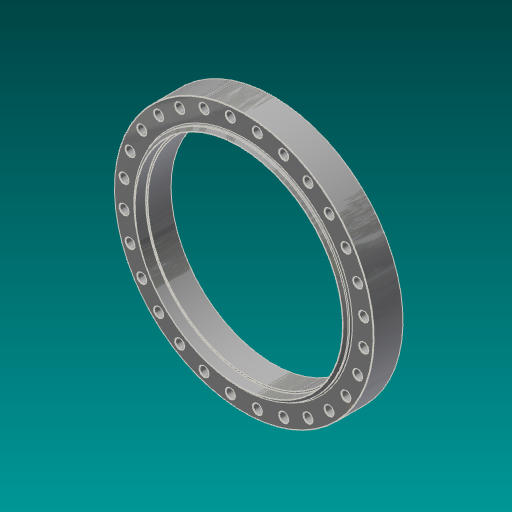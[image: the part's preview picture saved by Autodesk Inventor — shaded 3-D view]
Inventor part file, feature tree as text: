
AUTODESK INVENTOR PART (.ipt)
format: ipt  version: 2017.3 (Build 213257000, 257)  size: 330,240 bytes
history: native  units: in
note: dims shown in document units (in); Inventor stores cm internally (conversion verified against a paired STEP export)
features: chamfer x3, sketch x3, revolve x1, hole x1, pattern_circular x1, extrude x1, fillet x1
ambient origin geometry x8: Origin, YZ Plane, XZ Plane, XY Plane, X Axis, Y Axis, Z Axis, Center Point
bodies: Solid1 (feature_tree)
feature tree (11):
  revolve  "Revolution1"  [1 undecoded]
  hole  "Hole1"  [1 undecoded]
  chamfer  "Chamfer1"  Distance=32.0in
  pattern_circular  "Circular Pattern1"  [2 undecoded]
  chamfer  "Chamfer2"  Distance=32.0in
  extrude  "Extrusion1"  Depth=0.0312in
  fillet  "Fillet1"  Radius=0.4375in
  chamfer  "Chamfer3"  Distance=0.2in
  sketch  "Sketch1"  dims[d0=5.125in d1=38.75in]
  sketch  "Sketch2"  dims[d2=4.375in d3=33.75in]
  sketch  "Sketch3"  dims[d4=0.0625in d5=32.0in d6=31.0in d7=32.0in d8=0.2577in d9=0.4375in d10=0.2in d11=90.0deg d12=36.0in d13=0.0442in d14=1.375in d15=0.75in d16=0.375in d17=0.25in d18=0.5635in d19=1.0in d20=0.8108in d21=0.0625in d22=0.125in d23=45.0deg d24=11.0236in d25=360.0deg d27=0.0625in d28=0.125in d29=45.0deg d30=30.5in d31=3.5in d32=0.0in d33=0.0312in d34=0.0312in d35=0.125in d36=45.0deg]
note: 4 required parameter values undecoded (feature->parameter linkage not recoverable at this tier; creation-order binding heuristic only, values carry confidence <= 0.55)